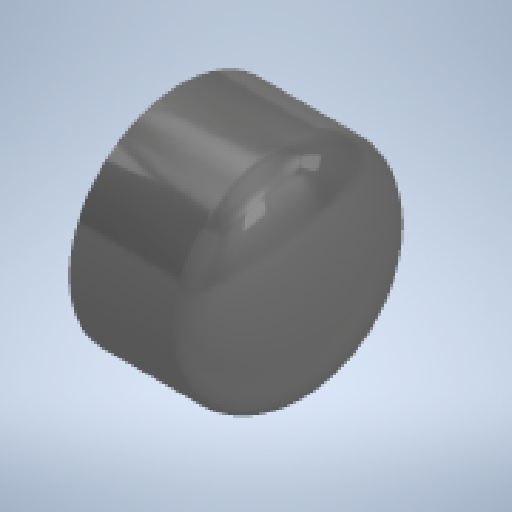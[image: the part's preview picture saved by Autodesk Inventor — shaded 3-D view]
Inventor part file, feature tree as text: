
AUTODESK INVENTOR PART (.ipt)
format: ipt  version: 2025 (Build 290162010, 162A)  size: 263,680 bytes
history: native  units: in
note: dims shown in document units (in); Inventor stores cm internally (conversion verified against a paired STEP export)
features: other x1, revolve x1
ambient origin geometry x8: Origin, YZ Plane, XZ Plane, XY Plane, X Axis, Y Axis, Z Axis, Center Point
bodies: Solid1 (feature_tree)
feature tree (2):
  other  "Axis1"
  revolve  "Revolve1"  [1 undecoded]
note: 1 required parameter value undecoded (feature->parameter linkage not recoverable at this tier; creation-order binding heuristic only, values carry confidence <= 0.55)
